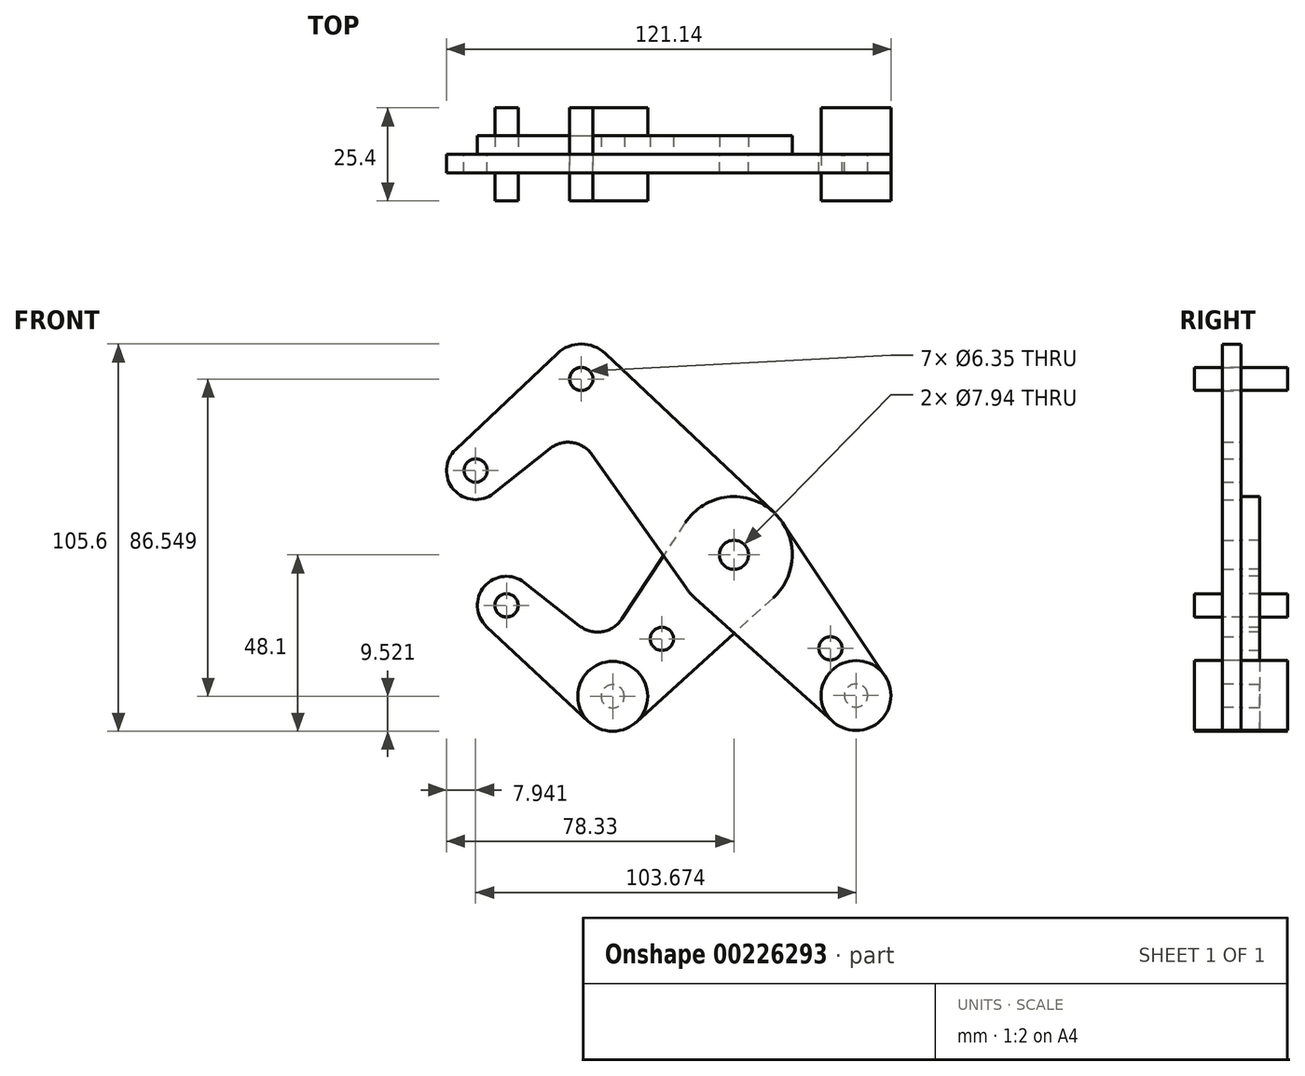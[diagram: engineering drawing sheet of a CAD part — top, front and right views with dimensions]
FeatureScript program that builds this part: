
annotation { "Feature Type Name" : "Feature", "Feature Type Description" : "" }
export const myFeature = defineFeature(function(context is Context, id is Id, definition is map)
    precondition{}
    {
        {
            var Q0;
            Q0=qCreatedBy(makeId("Front.planeOp"),FACE);
            var sketch = newSketch(context, id + "F0", { "sketchPlane" : qUnion([Q0])});
            skLineSegment(sketch, "E0", {"start": v(-41.6, 47.97) * mm, "end": v(41.6, -47.97) * mm, "construction": true});
            skCircle(sketch, "E1", {"center": v(0, 0) * mm, "radius": 3.18 * mm});
            skCircle(sketch, "E2", {"center": v(33.29, -38.38) * mm, "radius": 3.18 * mm});
            skCircle(sketch, "E3", {"center": v(-41.6, 47.97) * mm, "radius": 3.18 * mm});
            skCircle(sketch, "E4", {"center": v(-70.39, 23) * mm, "radius": 3.18 * mm});
            skLineSegment(sketch, "E5", {"start": v(-41.6, 47.97) * mm, "end": v(-70.39, 23) * mm, "construction": true});
            skCircle(sketch, "E6", {"center": v(33.29, -38.38) * mm, "radius": 9.53 * mm});
            skCircle(sketch, "E7", {"center": v(-70.39, 23) * mm, "radius": 7.94 * mm});
            skCircle(sketch, "E8", {"center": v(-41.6, 47.97) * mm, "radius": 9.53 * mm});
            skLineSegment(sketch, "E9", {"start": v(-75.83, 28.78) * mm, "end": v(-48.14, 54.9) * mm});
            skLineSegment(sketch, "E10", {"start": v(-65.44, 16.8) * mm, "end": v(-50.15, 28.98) * mm});
            skCircle(sketch, "E11", {"center": v(0, 0) * mm, "radius": 15.88 * mm});
            skLineSegment(sketch, "E12", {"start": v(-35.07, 54.9) * mm, "end": v(10.9, 11.55) * mm});
            skLineSegment(sketch, "E13", {"start": v(-38.72, 27.35) * mm, "end": v(-12.97, -9.15) * mm});
            skLineSegment(sketch, "E14", {"start": v(-10.6, -11.82) * mm, "end": v(26.93, -45.47) * mm});
            skLineSegment(sketch, "E15", {"start": v(13.2, 8.82) * mm, "end": v(41.2, -33.08) * mm});
            skArc(sketch, "E16.filletArc", {"start": v(-38.72, 27.35) * mm, "mid": v(-44.08, 30.63) * mm, "end": v(-50.15, 28.98) * mm});
            skLineSegment(sketch, "E17", {"start": v(0, 0) * mm, "end": v(-33.05, -38.58) * mm, "construction": true});
            skLineSegment(sketch, "E18", {"start": v(-33.05, -38.58) * mm, "end": v(-61.98, -13.8) * mm, "construction": true});
            skCircle(sketch, "E19", {"center": v(-61.98, -13.8) * mm, "radius": 3.18 * mm});
            skCircle(sketch, "E20", {"center": v(-33.05, -38.58) * mm, "radius": 3.18 * mm});
            skCircle(sketch, "E21", {"center": v(-61.98, -13.8) * mm, "radius": 7.94 * mm});
            skCircle(sketch, "E22", {"center": v(-33.05, -38.58) * mm, "radius": 9.53 * mm});
            skLineSegment(sketch, "E23", {"start": v(-57.08, -7.55) * mm, "end": v(-42.08, -19.35) * mm});
            skLineSegment(sketch, "E24", {"start": v(-67.4, -19.6) * mm, "end": v(-39.54, -45.55) * mm});
            skLineSegment(sketch, "E25", {"start": v(-13.25, 8.74) * mm, "end": v(-30.55, -17.48) * mm});
            skLineSegment(sketch, "E26", {"start": v(10.67, -11.75) * mm, "end": v(-26.65, -45.63) * mm});
            skArc(sketch, "E27.filletArc", {"start": v(-42.08, -19.35) * mm, "mid": v(-35.9, -20.95) * mm, "end": v(-30.55, -17.48) * mm});
            skCircle(sketch, "E28", {"center": v(-19.62, -22.9) * mm, "radius": 3.18 * mm});
            skCircle(sketch, "E29", {"center": v(26.32, -25.5) * mm, "radius": 3.18 * mm});
            skLineSegment(sketch, "E30", {"start": v(26.32, -25.5) * mm, "end": v(23.92, -27.58) * mm, "construction": true});
            skCircle(sketch, "E31", {"center": v(0, 0) * mm, "radius": 3.97 * mm});
            skSolve(sketch);
        }
        {
            var Q0;
            Q0=qCreatedBy(makeId("Front.planeOp"),FACE);
            cPlane(context, id + "F1", {"entities" : qUnion([Q0]), "cplaneType" : CPlaneType.OFFSET, "offset" : 12.7 * mm, "width" : 254 * mm, "height" : 254 * mm});
        }
        {
            var Q0;
            {var subQ1=sQuery(id+"F0.wireOp",EDGE,"E9");Q0=makeQuery(id+"F0.imprint","IMPRINT",FACE,{"disambiguationData":[TD([[makeQuery(id+"F0.imprint","IMPRINT",EDGE,{"derivedFrom":subQ1}),-1.0]])]});}
            var Q1;
            Q1=makeQuery(id+"F0.imprint","IMPRINT",FACE,{"disambiguationData":[TD([[makeQuery(id+"F0.imprint","IMPRINT",EDGE,{"derivedFrom":sQuery(id+"F0.wireOp",EDGE,"E3")}),-1.0]])]});
            var Q2;
            Q2=makeQuery(id+"F0.imprint","IMPRINT",FACE,{"disambiguationData":[TD([[makeQuery(id+"F0.imprint","IMPRINT",EDGE,{"derivedFrom":sQuery(id+"F0.wireOp",EDGE,"E4")}),-1.0]])]});
            var Q3;
            Q3=makeQuery(id+"F0.imprint","IMPRINT",FACE,{"disambiguationData":[TD([[makeQuery(id+"F0.imprint","IMPRINT",EDGE,{"derivedFrom":sQuery(id+"F0.wireOp",EDGE,"E31")}),-1.0]])]});
            var Q4;
            {var subQ0=sQuery(id+"F0.wireOp",EDGE,"E14");var subQ1=sQuery(id+"F0.wireOp",EDGE,"E11");var subQ2=makeQuery(id+"F0.imprint","INTERSECT",VERTEX,{"derivedFrom":[subQ1,subQ0]});Q4=makeQuery(id+"F0.imprint","IMPRINT",FACE,{"disambiguationData":[TD([[makeQuery(id+"F0.imprint","IMPRINT",EDGE,{"disambiguationData":[TD([[subQ2,-1.0]])],"derivedFrom":subQ1}),-1.0]])]});}
            var Q5;
            {var subQ0=sQuery(id+"F0.wireOp",EDGE,"E13");var subQ1=sQuery(id+"F0.wireOp",EDGE,"E11");var subQ2=makeQuery(id+"F0.imprint","INTERSECT",VERTEX,{"derivedFrom":[subQ1,subQ0]});Q5=makeQuery(id+"F0.imprint","IMPRINT",FACE,{"disambiguationData":[TD([[makeQuery(id+"F0.imprint","IMPRINT",EDGE,{"disambiguationData":[TD([[subQ2,1.0]])],"derivedFrom":subQ1}),-1.0]])]});}
            var Q6;
            {var subQ0=sQuery(id+"F0.wireOp",EDGE,"E15");Q6=makeQuery(id+"F0.imprint","IMPRINT",FACE,{"disambiguationData":[TD([[makeQuery(id+"F0.imprint","IMPRINT",EDGE,{"derivedFrom":subQ0}),-1.0]])]});}
            var Q7;
            Q7=makeQuery(id+"F0.imprint","IMPRINT",FACE,{"disambiguationData":[TD([[makeQuery(id+"F0.imprint","IMPRINT",EDGE,{"derivedFrom":sQuery(id+"F0.wireOp",EDGE,"E2")}),-1.0]])]});
            extrude(context, id + "F2", {"entities" : qUnion([Q0, Q1, Q2, Q3, Q4, Q5, Q6, Q7]), "depth" : 5.08 * mm});
        }
        {
            var Q0;
            Q0=makeQuery(id+"F0.imprint","IMPRINT",FACE,{"disambiguationData":[TD([[makeQuery(id+"F0.imprint","IMPRINT",EDGE,{"derivedFrom":sQuery(id+"F0.wireOp",EDGE,"E31")}),-1.0]])]});
            var Q1;
            {var subQ0=sQuery(id+"F0.wireOp",EDGE,"E13");var subQ1=sQuery(id+"F0.wireOp",EDGE,"E11");var subQ2=makeQuery(id+"F0.imprint","INTERSECT",VERTEX,{"derivedFrom":[subQ1,subQ0]});Q1=makeQuery(id+"F0.imprint","IMPRINT",FACE,{"disambiguationData":[TD([[makeQuery(id+"F0.imprint","IMPRINT",EDGE,{"disambiguationData":[TD([[subQ2,1.0]])],"derivedFrom":subQ1}),-1.0]])]});}
            var Q2;
            {var subQ0=sQuery(id+"F0.wireOp",EDGE,"E14");var subQ1=sQuery(id+"F0.wireOp",EDGE,"E11");var subQ2=makeQuery(id+"F0.imprint","INTERSECT",VERTEX,{"derivedFrom":[subQ1,subQ0]});Q2=makeQuery(id+"F0.imprint","IMPRINT",FACE,{"disambiguationData":[TD([[makeQuery(id+"F0.imprint","IMPRINT",EDGE,{"disambiguationData":[TD([[subQ2,-1.0]])],"derivedFrom":subQ1}),-1.0]])]});}
            var Q3;
            {var subQ10=sQuery(id+"F0.wireOp",EDGE,"E23");Q3=makeQuery(id+"F0.imprint","IMPRINT",FACE,{"disambiguationData":[TD([[makeQuery(id+"F0.imprint","IMPRINT",EDGE,{"derivedFrom":subQ10}),-1.0]])]});}
            var Q4;
            Q4=makeQuery(id+"F0.imprint","IMPRINT",FACE,{"disambiguationData":[TD([[makeQuery(id+"F0.imprint","IMPRINT",EDGE,{"derivedFrom":sQuery(id+"F0.wireOp",EDGE,"E19")}),-1.0]])]});
            var Q5;
            Q5=makeQuery(id+"F0.imprint","IMPRINT",FACE,{"disambiguationData":[TD([[makeQuery(id+"F0.imprint","IMPRINT",EDGE,{"derivedFrom":sQuery(id+"F0.wireOp",EDGE,"E20")}),-1.0]])]});
            extrude(context, id + "F3", {"entities" : qUnion([Q0, Q1, Q2, Q3, Q4, Q5]), "oppositeDirection" : true, "depth" : 5.08 * mm});
        }
        {
            var Q0;
            Q0=qCreatedBy(id+"F1.planeOp",FACE);
            var sketch = newSketch(context, id + "F4", { "sketchPlane" : qUnion([Q0])});
            skArc(sketch, "E32.0.0", {"start": v(26.93, -45.47) * mm, "mid": v(39.53, -45.57) * mm, "end": v(41.2, -33.08) * mm});
            skArc(sketch, "E32.0.1", {"start": v(41.2, -33.08) * mm, "mid": v(27.04, -31.18) * mm, "end": v(26.93, -45.47) * mm});
            skCircle(sketch, "E33", {"center": v(-41.6, 47.97) * mm, "radius": 3.15 * mm});
            skSolve(sketch);
        }
        {
            var Q0;
            Q0=qCreatedBy(id+"F1.planeOp",FACE);
            var sketch = newSketch(context, id + "F5", { "sketchPlane" : qUnion([Q0])});
            skCircle(sketch, "E34.0", {"center": v(-33.05, -38.58) * mm, "radius": 9.53 * mm});
            skCircle(sketch, "E35", {"center": v(-61.98, -13.79) * mm, "radius": 3.15 * mm});
            skSolve(sketch);
        }
        {
            var Q0;
            Q0 = qSketchRegion(id + "F4", true);
            var Q1;
            Q1 = qSketchRegion(id + "F5", true);
            var Q2;
            Q2=qCreatedBy(id+"F1.planeOp",FACE);
            extrude(context, id + "F6", {"entities" : qUnion([Q0, Q1]), "oppositeDirection" : true, "endBoundEntityFace" : qUnion([Q2]), "depth" : 25.4 * mm});
        }
    });
